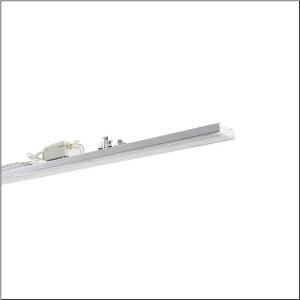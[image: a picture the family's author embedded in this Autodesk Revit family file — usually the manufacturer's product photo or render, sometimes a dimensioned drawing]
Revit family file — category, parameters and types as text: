
# Revit family: licross_r__21_recessed_ho_52tl1edn4e5s_7fa6
name_source: partatom
category: Lighting Fixtures
units: mm (PartAtom-declared; Revit-internal decimal feet)

## family parameters
Cut with Voids When Loaded = No
Host = Face
Light Source = No
Part Type = Normal
Room Calculation Point = No
Round Connector Dimension = Use Diameter
Shared = No

## types (1)
- --- (1 x LED, 14620 lm, 84.6 W, 4000K)
    Apparent Load = 85 VA
    CIE Flux Codes = 85 95 99 100 100
    Color Rendering = 80
    Color Temperature = 4000K
    Default Elevation = 1800 mm
    Description = Licross® 21 Recessed HO, luminaire insert, of sheet steel, galvanised, coil coated, white, length: 1.500mm, width: 66mm, height: 67mm, LED rated luminous flux: 14.620lm, light colour: 840, control gear: DALI 2, with plug, 5-pole, with phase selection, mains connection: 220..240V, AC, 50/60Hz, rated input power: 85W, halogen-free wiring, primary light control with lens, of plastic, primary optical cover: cover, of PMMA, light emission: direct distribution, primary light characteristic: symmetric, protection rating (complete): IP40, insulation class (complete): insulation class I (protective earthing), certification: CE, ENEC, VDE, UKCA, protection symbol: D if used in an environment without relevant dust loads with corresponding accessories, impact resistance: IK06, permissible ambient temperature for indoor applications: -25..+30°C, corresponds to IFS (International Featured Standards) requirements for safety and quality in the food industry, reducing of maximum allowable ambient temperature of 5°C with ceiling mounting, LABS conformity tested according to VDMA 24364:2018-05, packaging unit: 1 piece
    Height = 58 mm
    Lamp = 1 x LED
    Lamp Light Flux = 14620 lm
    Lamp Power = 84.6 W
    Lamp count = 1
    Length = 1500 mm
    Luminous efficacy = 173 lm/W
    Manufacturer = Siteco
    ModVariant = No
    Model = 52TL1EDN4E5S
    Mounting Place = Ceiling
    Mounting Type = Pendant
    Number of Poles = 1
    OnlyDefault = Yes
    Power Factor = 1
    Product Name = Licross® 21 Recessed HO
    Product group = luminaire insert
    ProductGroupID = 901
    Protection Class = Protection class I
    Protection Degree = IP 40
    RLX_Detail_Level = 1
    RLX_Emergency_Light_Flux = 0 lm
    RLX_Emergency_Type = 0
    RLX_Emergency_Type_DB = No
    RlxData = <blob elided: 24757 chars, md5=4b594ff7>
    Socket = socket
    Standby Power = 0 W
    System Light Flux = 14620 lm
    System Power = 85 W
    Type Comments = factory setting: luminous flux: 100 % | dim-lin: 254 | 484 mA
    Type Image = l_1296930.jpg
    URL = http://relux.com
    VarID = @adj_056713
    Voltage = 0 V
    Weight = 0.00 kg
    Width = 66 mm

## geometry (parser evidence)
native form markers: Blend x4, Sweep x11
no freeform markers — native parametric forms only
